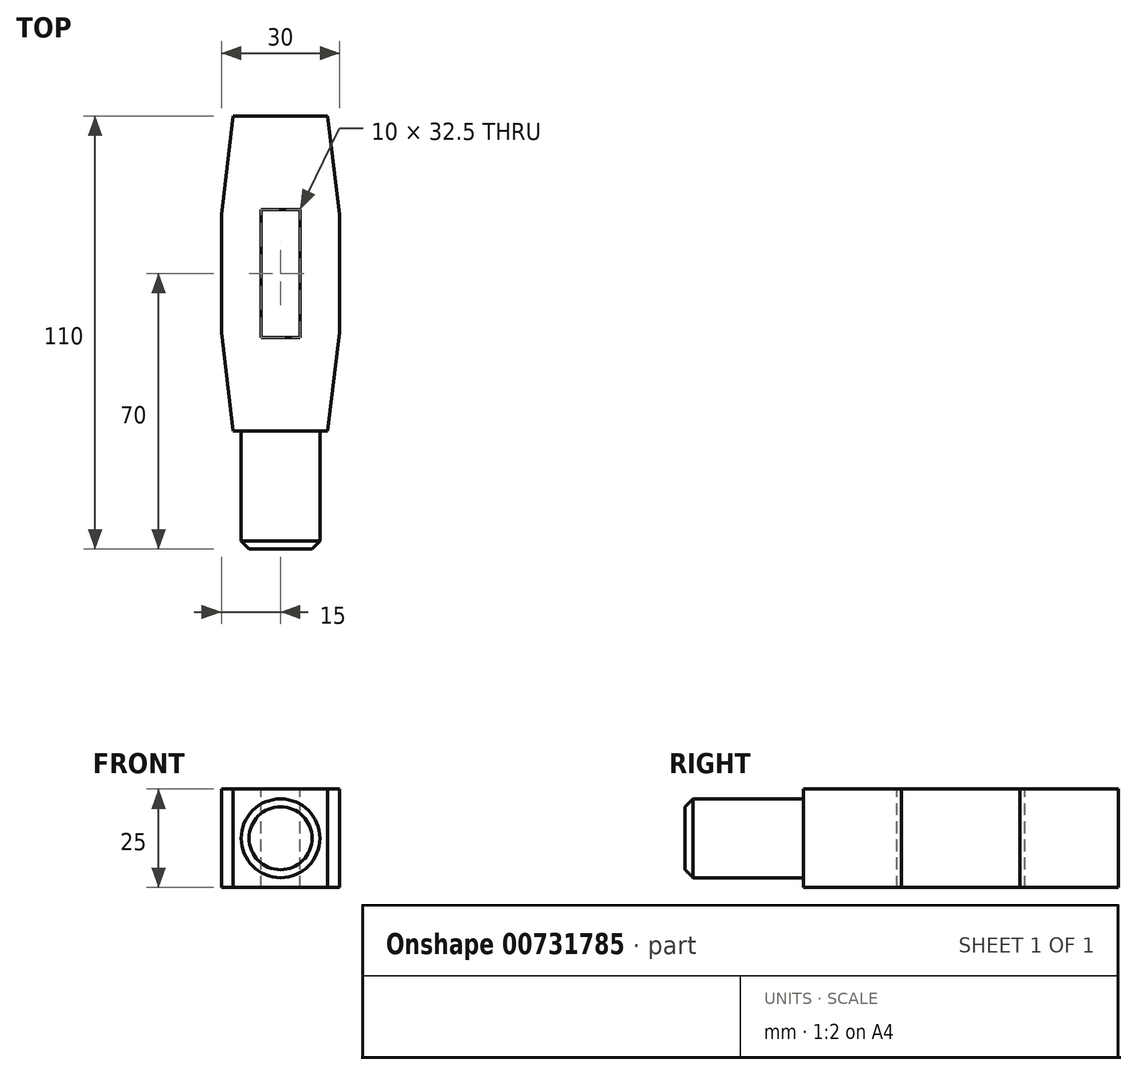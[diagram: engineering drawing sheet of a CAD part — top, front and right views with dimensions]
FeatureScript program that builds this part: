
annotation { "Feature Type Name" : "Feature", "Feature Type Description" : "" }
export const myFeature = defineFeature(function(context is Context, id is Id, definition is map)
    precondition{}
    {
        {
            var Q0;
            Q0=qCreatedBy(makeId("Top.planeOp"),FACE);
            var sketch = newSketch(context, id + "F0", { "sketchPlane" : qUnion([Q0])});
            skLineSegment(sketch, "E0", {"start": v(-12, -40) * mm, "end": v(12, -40) * mm});
            skLineSegment(sketch, "E1", {"start": v(12, -40) * mm, "end": v(15, -15) * mm});
            skLineSegment(sketch, "E2", {"start": v(15, -15) * mm, "end": v(15, 15) * mm});
            skLineSegment(sketch, "E3", {"start": v(15, 15) * mm, "end": v(12, 40) * mm});
            skLineSegment(sketch, "E4", {"start": v(12, 40) * mm, "end": v(-12, 40) * mm});
            skLineSegment(sketch, "E5", {"start": v(-12, 40) * mm, "end": v(-15, 15) * mm});
            skLineSegment(sketch, "E6", {"start": v(-15, 15) * mm, "end": v(-15, -15) * mm});
            skLineSegment(sketch, "E7", {"start": v(-15, -15) * mm, "end": v(-12, -40) * mm});
            skSolve(sketch);
        }
        {
            var Q0;
            Q0=makeQuery(id+"F0.imprint","IMPRINT",FACE,{"disambiguationData":[TD([[makeQuery(id+"F0.imprint","IMPRINT",EDGE,{"derivedFrom":sQuery(id+"F0.wireOp",EDGE,"E0")}),1.0]])]});
            extrude(context, id + "F1", {"entities" : qUnion([Q0]), "endBound" : BoundingType.SYMMETRIC, "depth" : 25 * mm, "offsetDistance" : 25 * mm});
        }
        {
            var Q0;
            Q0=makeQuery(id+"F1.opExtrude","SWEPT_FACE",FACE,{"disambiguationData":[OSD([sQuery(id+"F0.wireOp",EDGE,"E0")])]});
            var sketch = newSketch(context, id + "F2", { "sketchPlane" : qUnion([Q0])});
            skCircle(sketch, "E8", {"center": v(0, 0) * mm, "radius": 10 * mm});
            skSolve(sketch);
        }
        {
            var Q0;
            Q0 = qSketchRegion(id + "F2", true);
            extrude(context, id + "F3", {"entities" : qUnion([Q0]), "operationType" : NewBodyOperationType.ADD, "depth" : 30 * mm, "offsetDistance" : 25 * mm});
        }
        {
            var Q0;
            Q0=makeQuery(id+"F3.opExtrude","CAP_EDGE",EDGE,{"disambiguationData":[OSD([sQuery(id+"F2.wireOp",EDGE,"E8")])],"isStart":false});
            chamfer(context, id + "F4", {"entities" : qUnion([Q0]), "width" : 2 * mm, "tangentPropagation" : true});
        }
        {
            var Q0;
            Q0=makeQuery(id+"F1.opExtrude","CAP_FACE",FACE,{"disambiguationData":[OSD([sQuery(id+"F0.wireOp",EDGE,"E0"),sQuery(id+"F0.wireOp",EDGE,"E1"),sQuery(id+"F0.wireOp",EDGE,"E2"),sQuery(id+"F0.wireOp",EDGE,"E3"),sQuery(id+"F0.wireOp",EDGE,"E4"),sQuery(id+"F0.wireOp",EDGE,"E5"),sQuery(id+"F0.wireOp",EDGE,"E6"),sQuery(id+"F0.wireOp",EDGE,"E7")])],"isStart":false});
            var sketch = newSketch(context, id + "F5", { "sketchPlane" : qUnion([Q0])});
            skLineSegment(sketch, "E9.bottom", {"start": v(-5, 16.25) * mm, "end": v(5, 16.25) * mm});
            skLineSegment(sketch, "E9.top", {"start": v(-5, -16.25) * mm, "end": v(5, -16.25) * mm});
            skLineSegment(sketch, "E9.left", {"start": v(-5, 16.25) * mm, "end": v(-5, -16.25) * mm});
            skLineSegment(sketch, "E9.right", {"start": v(5, 16.25) * mm, "end": v(5, -16.25) * mm});
            skSolve(sketch);
        }
        {
            var Q0;
            Q0 = qSketchRegion(id + "F5", true);
            extrude(context, id + "F6", {"entities" : qUnion([Q0]), "operationType" : NewBodyOperationType.REMOVE, "oppositeDirection" : true, "depth" : 25 * mm, "offsetDistance" : 25 * mm});
        }
    });
